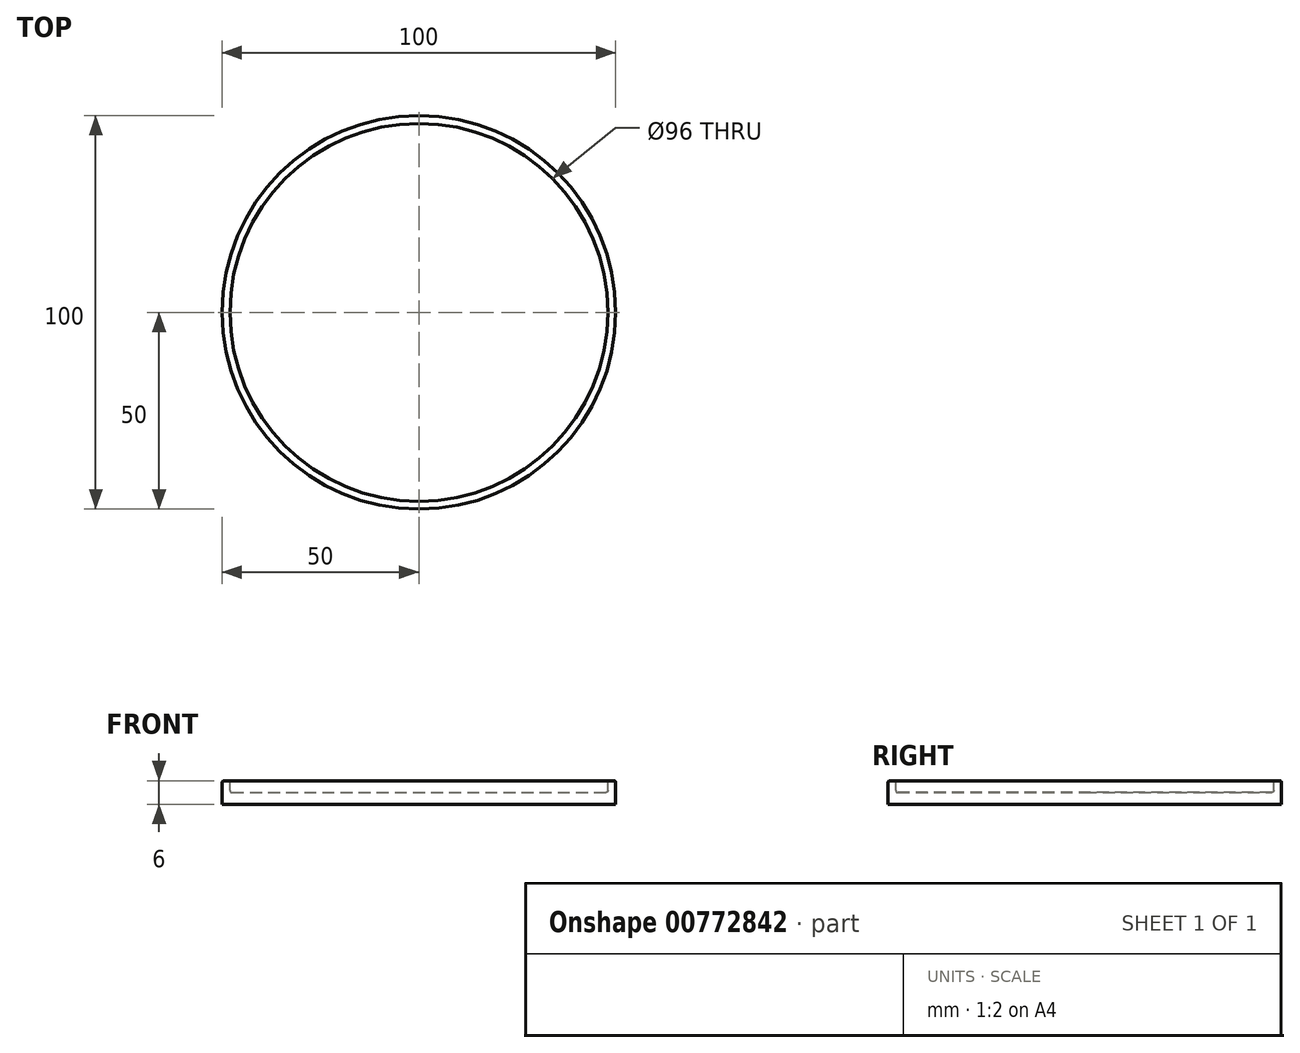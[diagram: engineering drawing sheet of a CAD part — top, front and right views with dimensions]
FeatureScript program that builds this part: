
annotation { "Feature Type Name" : "Feature", "Feature Type Description" : "" }
export const myFeature = defineFeature(function(context is Context, id is Id, definition is map)
    precondition{}
    {
        {
            var Q0;
            Q0=qCreatedBy(makeId("Front.planeOp"),FACE);
            var sketch = newSketch(context, id + "F0", { "sketchPlane" : qUnion([Q0])});
            skLineSegment(sketch, "E0", {"start": v(0, 0) * mm, "end": v(-50, 0) * mm});
            skLineSegment(sketch, "E1", {"start": v(-50, 0) * mm, "end": v(-50, 6) * mm});
            skLineSegment(sketch, "E2", {"start": v(-50, 6) * mm, "end": v(-48, 6) * mm});
            skLineSegment(sketch, "E3", {"start": v(-48, 6) * mm, "end": v(-48, 3) * mm});
            skLineSegment(sketch, "E4", {"start": v(-48, 3) * mm, "end": v(0, 3) * mm});
            skLineSegment(sketch, "E5", {"start": v(0, 3) * mm, "end": v(0, 0) * mm});
            skSolve(sketch);
        }
        {
            var Q0;
            Q0=qSketchRegion(id+"F0",true);
            var Q1;
            Q1=sQuery(id+"F0.wireOp",EDGE,"E5");
            revolve(context, id + "F1", {"surfaceOperationType" : NewSurfaceOperationType.NEW, "entities" : qUnion([Q0]), "axis" : qUnion([Q1]), "revolveType" : RevolveType.FULL});
        }
        {
            var Q0;
            Q0=makeQuery(id+"F1.opRevolve","SWEPT_EDGE",EDGE,{"disambiguationData":[OSD([sQuery(id+"F0.wireOp",EDGE,"E1"),sQuery(id+"F0.wireOp",EDGE,"E2")])]});
            fillet(context, id + "F2", {"entities" : qUnion([Q0]), "radius" : .5 * mm, "tangentPropagation" : true, "allowEdgeOverflow" : false});
        }
        {
            var Q0;
            Q0=makeQuery(id+"F1.opRevolve","SWEPT_EDGE",EDGE,{"disambiguationData":[OSD([sQuery(id+"F0.wireOp",EDGE,"E2"),sQuery(id+"F0.wireOp",EDGE,"E3")])]});
            fillet(context, id + "F3", {"entities" : qUnion([Q0]), "radius" : .5 * mm, "tangentPropagation" : true, "allowEdgeOverflow" : false});
        }
        {
            var Q0;
            Q0=makeQuery(id+"F1.opRevolve","SWEPT_EDGE",EDGE,{"disambiguationData":[OSD([sQuery(id+"F0.wireOp",EDGE,"E3"),sQuery(id+"F0.wireOp",EDGE,"E4")])]});
            fillet(context, id + "F4", {"entities" : qUnion([Q0]), "radius" : .5 * mm, "tangentPropagation" : true, "allowEdgeOverflow" : false});
        }
    });
